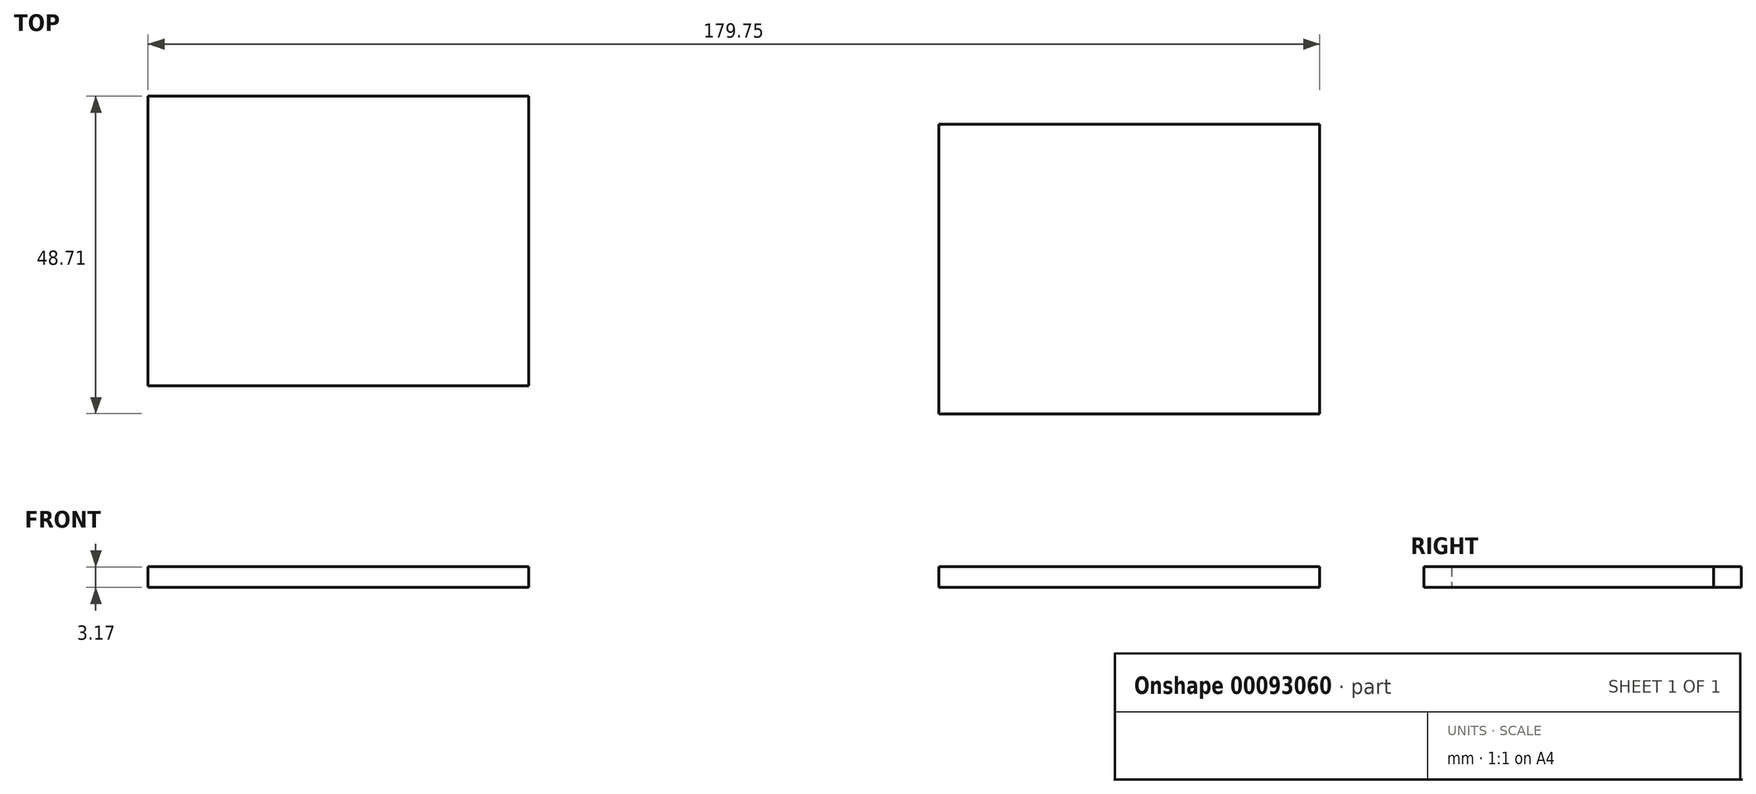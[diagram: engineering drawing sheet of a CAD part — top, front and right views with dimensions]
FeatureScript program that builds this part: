
annotation { "Feature Type Name" : "Feature", "Feature Type Description" : "" }
export const myFeature = defineFeature(function(context is Context, id is Id, definition is map)
    precondition{}
    {
        {
            var Q0;
            Q0=qCreatedBy(makeId("Top.planeOp"),FACE);
            var sketch = newSketch(context, id + "F0", { "sketchPlane" : qUnion([Q0])});
            skLineSegment(sketch, "E0.bottom", {"start": v(-33.39, 32.65) * mm, "end": v(25.03, 32.65) * mm});
            skLineSegment(sketch, "E0.top", {"start": v(-33.39, -11.8) * mm, "end": v(25.03, -11.8) * mm});
            skLineSegment(sketch, "E0.left", {"start": v(-33.39, 32.65) * mm, "end": v(-33.39, -11.8) * mm});
            skLineSegment(sketch, "E0.right", {"start": v(25.03, 32.65) * mm, "end": v(25.03, -11.8) * mm});
            skLineSegment(sketch, "E1.bottom", {"start": v(-154.72, 36.91) * mm, "end": v(-96.3, 36.91) * mm});
            skLineSegment(sketch, "E1.top", {"start": v(-154.72, -7.54) * mm, "end": v(-96.3, -7.54) * mm});
            skLineSegment(sketch, "E1.left", {"start": v(-154.72, 36.91) * mm, "end": v(-154.72, -7.54) * mm});
            skLineSegment(sketch, "E1.right", {"start": v(-96.3, 36.91) * mm, "end": v(-96.3, -7.54) * mm});
            skSolve(sketch);
        }
        {
            var Q0;
            Q0=makeQuery(id+"F0.imprint","IMPRINT",FACE,{"disambiguationData":[TD([[makeQuery(id+"F0.imprint","IMPRINT",EDGE,{"derivedFrom":sQuery(id+"F0.wireOp",EDGE,"E0.bottom")}),-1.0]])]});
            var Q1;
            Q1=makeQuery(id+"F0.imprint","IMPRINT",FACE,{"disambiguationData":[TD([[makeQuery(id+"F0.imprint","IMPRINT",EDGE,{"derivedFrom":sQuery(id+"F0.wireOp",EDGE,"E1.bottom")}),-1.0]])]});
            extrude(context, id + "F1", {"entities" : qUnion([Q0, Q1]), "depth" : 3.17 * mm});
        }
    });
